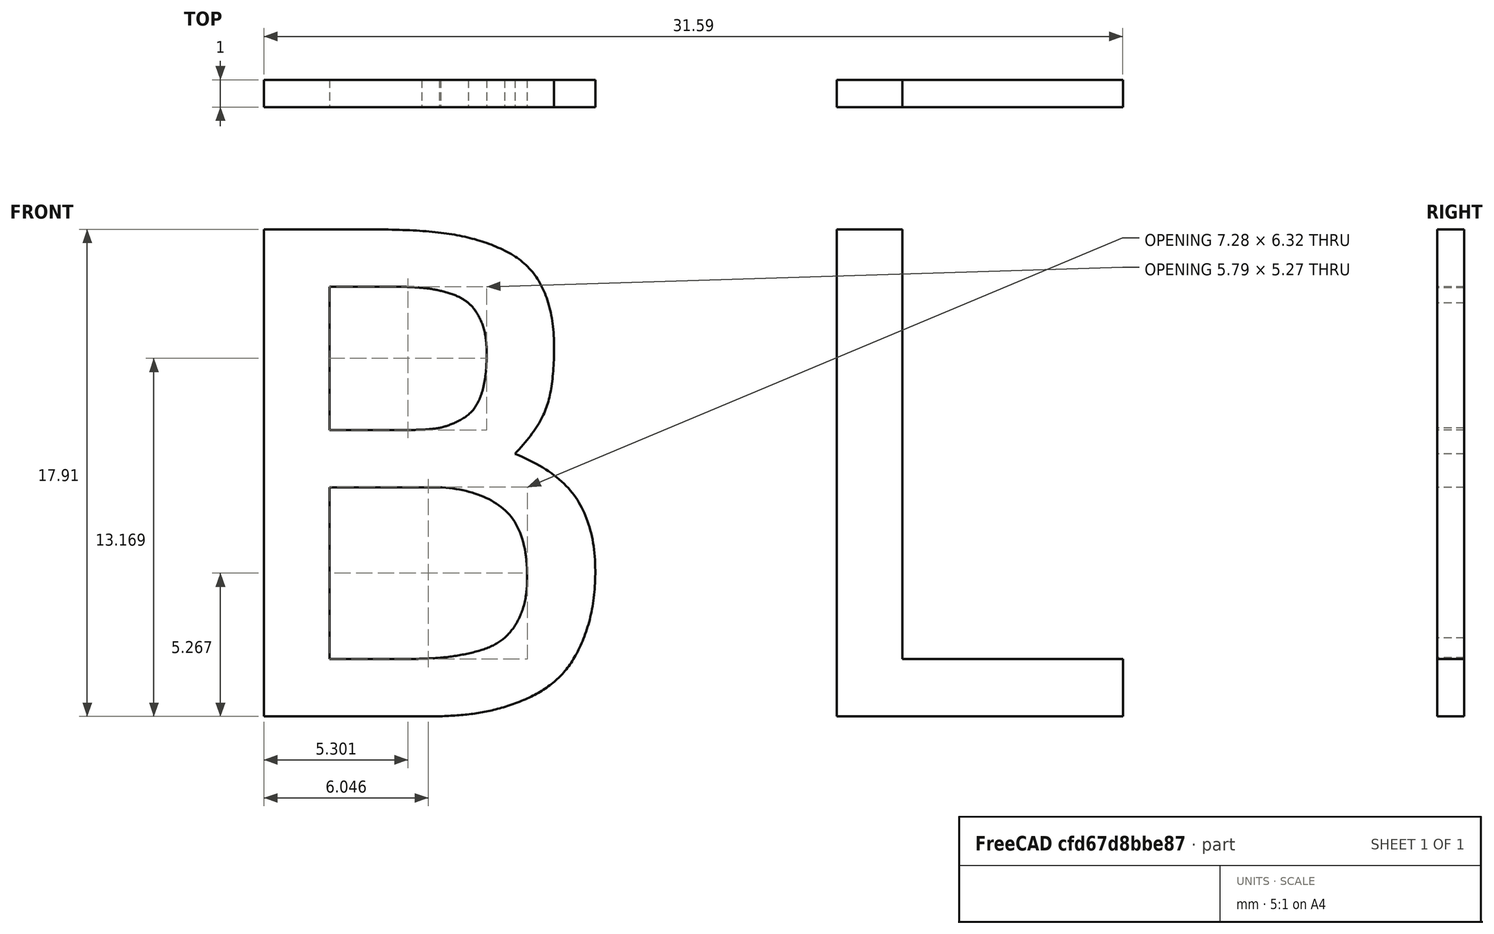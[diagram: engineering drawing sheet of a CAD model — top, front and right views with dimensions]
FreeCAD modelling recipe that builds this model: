
FCSTD DOCUMENT  (FreeCAD 0.18R16131 (Git))
Label: InterupteurTerrasse
License: All rights reserved
LicenseURL: http://en.wikipedia.org/wiki/All_rights_reserved
objects: Part::Part2DObjectPython×2, Sketcher::SketchObject×1, PartDesign::Body×1, Part::Extrusion×1
note: 5 computed .brp shape members not serialized (recipe doc carries the construction recipe); baked Part::Feature solids carry a one-line shape summary decoded from their .brp

FEATURE [Sketcher::SketchObject] Sketch
  MapMode = 5
  Support = -> [XY_Plane]
FEATURE [PartDesign::Body] Body
  Group = -> [Sketch]
  Origin = -> Origin
FEATURE [Part::Part2DObjectPython] ShapeString001  # Draft 2D object (typed FeaturePython)
  FontFile = <path>
  Placement = pos=(-6.7,-14,-33.4) rot=(1,0,0;1.5708rad)
  Size = 10
  String = B L
  Tracking = 0
FEATURE [Part::Part2DObjectPython] Shape2DView  # Draft 2D object (typed FeaturePython)
  Base = -> ShapeString001
  HiddenLines = false
  InPlace = true
  Projection = (-0.329783,-0.741525,0.584281)
  ProjectionMode = 0
  SegmentLength = 0.05
  Tessellation = false
  VisibleOnly = false
FEATURE [Part::Extrusion] Extrude001
  Base = -> ShapeString001
  Dir = (0,-1,2e-16)
  DirMode = 2
  FaceMakerClass = Part::FaceMakerBullseye
  LengthFwd = 1
  LengthRev = 0
  Solid = false
  Symmetric = false
note: 1 file-system path scrubbed to <path> (originals preserved in the JSON sidecar)
